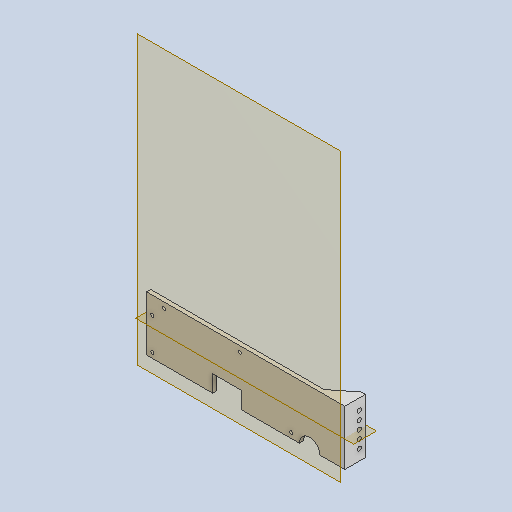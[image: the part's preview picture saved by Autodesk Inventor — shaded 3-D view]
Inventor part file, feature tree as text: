
AUTODESK INVENTOR PART (.ipt)
format: ipt  version: 2022 (Build 260153000, 153)  size: 157,696 bytes
history: native  units: in
note: dims shown in document units (in); Inventor stores cm internally (conversion verified against a paired STEP export)
features: other x6, sketch x6, reference x4, extrude x2, plane x2
ambient origin geometry x8: Origin, YZ Plane, XZ Plane, XY Plane, X Axis, Y Axis, Z Axis, Center Point
bodies: Solid1 (feature_tree)
feature tree (20):
  other  "dilution system bracket.ipt"
  extrude  "Extrusion1"  Depth=0.1969in
  extrude  "Extrusion2"  Depth=0.1969in
  other  "Solid1::dilution system bracket.ipt"
  other  "TaggingFeature1"
  sketch  "Sketch1"  dims[d0=0.3937in d1=0.1969in]
  sketch  "Sketch2"  dims[d2=0.1969in d3=0.1969in]
  sketch  "Sketch3"  dims[d4=0.0in d5=0.0in]
  sketch  "Sketch4"  dims[d6=0.9843in]
  plane  "Work Plane1"
  plane  "Work Plane2"
  sketch  "Sketch5"  dims[d7=0.0in d8=0.0in]
  reference  "Reference1"
  reference  "Reference2"
  reference  "Reference3"
  reference  "Reference4"
  sketch  "Sketch6"
  other  "Linear Rail Assembly.iam"
  other  "Printer Assembly:1"
  other  "Base_v7:1"
